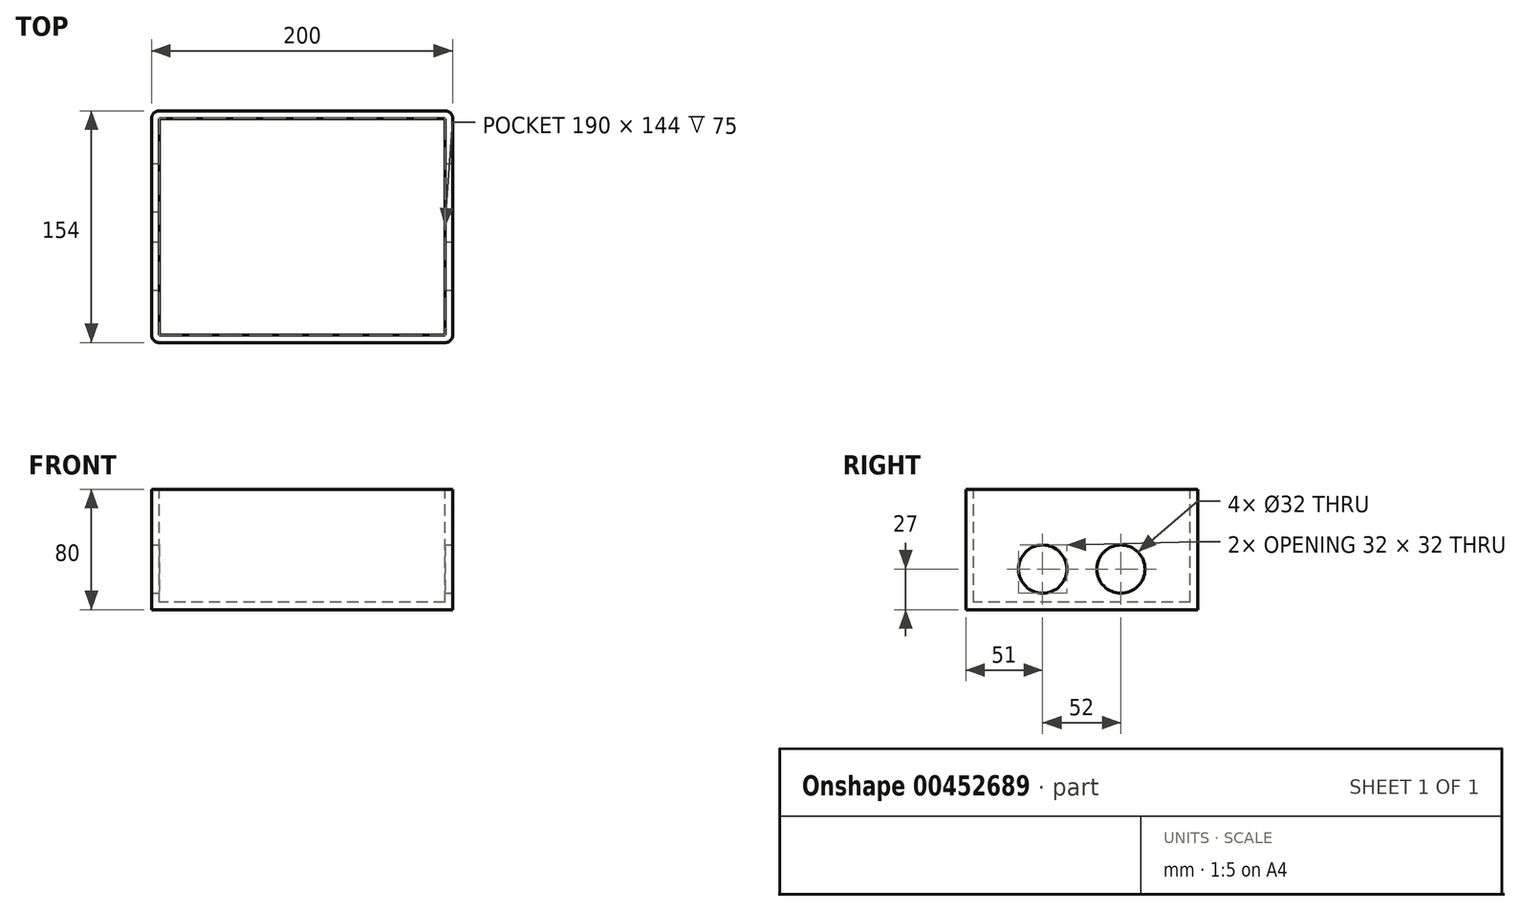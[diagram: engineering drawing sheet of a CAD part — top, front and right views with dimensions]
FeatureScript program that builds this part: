
annotation { "Feature Type Name" : "Feature", "Feature Type Description" : "" }
export const myFeature = defineFeature(function(context is Context, id is Id, definition is map)
    precondition{}
    {
        {
            var Q0;
            Q0=qCreatedBy(makeId("Top.planeOp"),FACE);
            var sketch = newSketch(context, id + "F0", { "sketchPlane" : qUnion([Q0])});
            skLineSegment(sketch, "E0.bottom", {"start": v(95, 77) * mm, "end": v(-95, 77) * mm});
            skLineSegment(sketch, "E0.top", {"start": v(95, -77) * mm, "end": v(-95, -77) * mm});
            skLineSegment(sketch, "E0.left", {"start": v(100, 72) * mm, "end": v(100, -72) * mm});
            skLineSegment(sketch, "E0.right", {"start": v(-100, 72) * mm, "end": v(-100, -72) * mm});
            skPoint(sketch, "E0.middle", {"position": v(0, 0) * mm});
            skPoint(sketch, "E1.visualSharp", {"position": v(-100, -77) * mm});
            skArc(sketch, "E1.filletArc", {"start": v(-100, -72) * mm, "mid": v(-98.54, -75.54) * mm, "end": v(-95, -77) * mm});
            skPoint(sketch, "E2.visualSharp", {"position": v(-100, 77) * mm});
            skArc(sketch, "E2.filletArc", {"start": v(-95, 77) * mm, "mid": v(-98.54, 75.54) * mm, "end": v(-100, 72) * mm});
            skPoint(sketch, "E3.visualSharp", {"position": v(100, 77) * mm});
            skArc(sketch, "E3.filletArc", {"start": v(100, 72) * mm, "mid": v(98.54, 75.54) * mm, "end": v(95, 77) * mm});
            skPoint(sketch, "E4.visualSharp", {"position": v(100, -77) * mm});
            skArc(sketch, "E4.filletArc", {"start": v(95, -77) * mm, "mid": v(98.54, -75.54) * mm, "end": v(100, -72) * mm});
            skSolve(sketch);
        }
        {
            var Q0;
            Q0=makeQuery(id+"F0.imprint","IMPRINT",FACE,{"disambiguationData":[TD([[makeQuery(id+"F0.imprint","IMPRINT",EDGE,{"derivedFrom":sQuery(id+"F0.wireOp",EDGE,"E0.bottom")}),1.0]])]});
            extrude(context, id + "F1", {"entities" : qUnion([Q0]), "depth" : 80 * mm});
        }
        {
            var Q0;
            Q0=makeQuery(id+"F1.opExtrude","CAP_FACE",FACE,{"disambiguationData":[OSD([sQuery(id+"F0.wireOp",EDGE,"E0.bottom"),sQuery(id+"F0.wireOp",EDGE,"E0.top"),sQuery(id+"F0.wireOp",EDGE,"E0.left"),sQuery(id+"F0.wireOp",EDGE,"E0.right")])],"isStart":false});
            var sketch = newSketch(context, id + "F2", { "sketchPlane" : qUnion([Q0])});
            skLineSegment(sketch, "E5.0", {"start": v(95, 72) * mm, "end": v(-95, 72) * mm});
            skLineSegment(sketch, "E5.1", {"start": v(95, 72) * mm, "end": v(95, -72) * mm});
            skLineSegment(sketch, "E5.2", {"start": v(95, -72) * mm, "end": v(-95, -72) * mm});
            skLineSegment(sketch, "E5.3", {"start": v(-95, 72) * mm, "end": v(-95, -72) * mm});
            skSolve(sketch);
        }
        {
            var Q0;
            Q0=makeQuery(id+"F2.imprint","IMPRINT",FACE,{"disambiguationData":[TD([[makeQuery(id+"F2.imprint","IMPRINT",EDGE,{"derivedFrom":sQuery(id+"F2.wireOp",EDGE,"E5.0")}),1.0]])]});
            extrude(context, id + "F3", {"entities" : qUnion([Q0]), "operationType" : NewBodyOperationType.REMOVE, "oppositeDirection" : true, "depth" : 75 * mm});
        }
        {
            var Q0;
            Q0=makeQuery(id+"F1.opExtrude","SWEPT_FACE",FACE,{"disambiguationData":[OSD([sQuery(id+"F0.wireOp",EDGE,"E0.left")])]});
            var sketch = newSketch(context, id + "F4", { "sketchPlane" : qUnion([Q0])});
            skCircle(sketch, "E6", {"center": v(26, 27) * mm, "radius": 16 * mm});
            skCircle(sketch, "E7", {"center": v(-26, 27) * mm, "radius": 16 * mm});
            skSolve(sketch);
        }
        {
            var Q0;
            Q0=makeQuery(id+"F4.imprint","IMPRINT",FACE,{"disambiguationData":[TD([[makeQuery(id+"F4.imprint","IMPRINT",EDGE,{"derivedFrom":sQuery(id+"F4.wireOp",EDGE,"E6")}),1.0]])]});
            var Q1;
            Q1=makeQuery(id+"F4.imprint","IMPRINT",FACE,{"disambiguationData":[TD([[makeQuery(id+"F4.imprint","IMPRINT",EDGE,{"derivedFrom":sQuery(id+"F4.wireOp",EDGE,"E7")}),1.0]])]});
            extrude(context, id + "F5", {"entities" : qUnion([Q0, Q1]), "operationType" : NewBodyOperationType.REMOVE, "endBound" : BoundingType.THROUGH_ALL, "oppositeDirection" : true, "depth" : 25 * mm});
        }
    });
